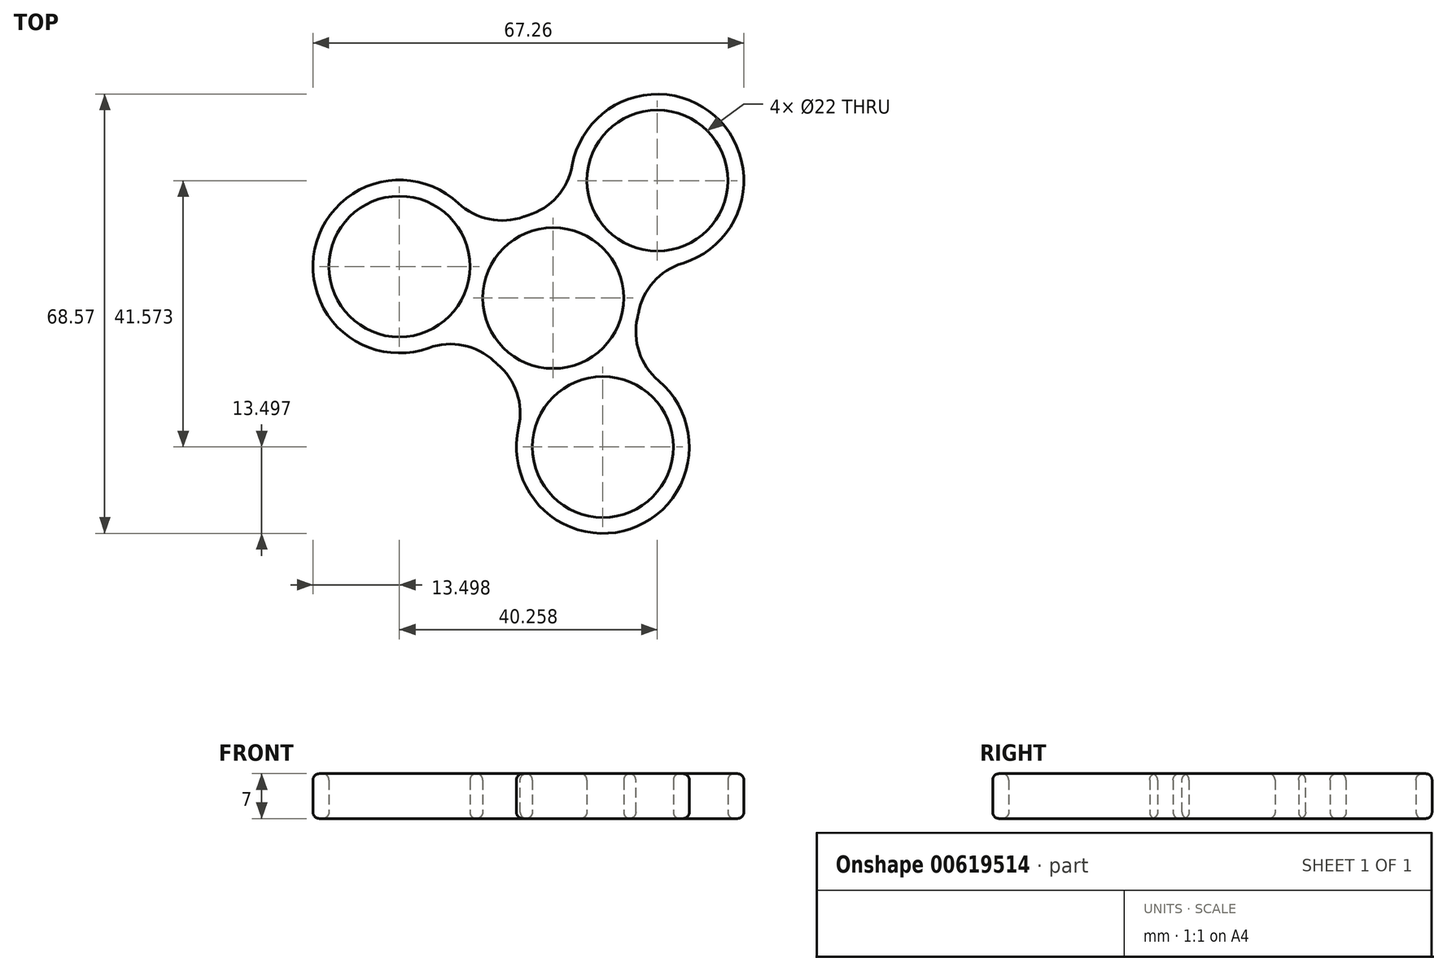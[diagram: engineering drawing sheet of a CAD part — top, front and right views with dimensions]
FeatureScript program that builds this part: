
annotation { "Feature Type Name" : "Feature", "Feature Type Description" : "" }
export const myFeature = defineFeature(function(context is Context, id is Id, definition is map)
    precondition{}
    {
        {
            var Q0;
            Q0=qCreatedBy(makeId("Top.planeOp"),FACE);
            var sketch = newSketch(context, id + "F0", { "sketchPlane" : qUnion([Q0])});
            skCircle(sketch, "E0", {"center": v(0, 0) * mm, "radius": 11 * mm});
            skCircle(sketch, "E1", {"center": v(0, 0) * mm, "radius": 13.5 * mm});
            skCircle(sketch, "E2", {"center": v(0, 0) * mm, "radius": 38 * mm});
            skCircle(sketch, "E3", {"center": v(16.26, 18.33) * mm, "radius": 13.5 * mm});
            skCircle(sketch, "E4", {"center": v(16.26, 18.33) * mm, "radius": 11 * mm});
            skCircle(sketch, "E5.1.0", {"center": v(-24, 4.91) * mm, "radius": 11 * mm});
            skCircle(sketch, "E5.1.1", {"center": v(-24, 4.91) * mm, "radius": 13.5 * mm});
            skCircle(sketch, "E5.2.0", {"center": v(7.75, -23.24) * mm, "radius": 11 * mm});
            skCircle(sketch, "E5.2.1", {"center": v(7.75, -23.24) * mm, "radius": 13.5 * mm});
            skSolve(sketch);
        }
        {
            var Q0;
            {var subQ0=sQuery(id+"F0.wireOp",EDGE,"E1");var subQ1=makeQuery(id+"F0.imprint","INTERSECT",VERTEX,{"derivedFrom":[subQ0,sQuery(id+"F0.wireOp",EDGE,"E5.1.0")]});Q0=makeQuery(id+"F0.imprint","IMPRINT",FACE,{"disambiguationData":[TD([[makeQuery(id+"F0.imprint","IMPRINT",EDGE,{"disambiguationData":[TD([[subQ1,1.0]])],"derivedFrom":subQ0}),1.0]])]});}
            var Q1;
            {var subQ0=sQuery(id+"F0.wireOp",EDGE,"E1");var subQ1=makeQuery(id+"F0.imprint","INTERSECT",VERTEX,{"derivedFrom":[subQ0,sQuery(id+"F0.wireOp",EDGE,"E4")]});Q1=makeQuery(id+"F0.imprint","IMPRINT",FACE,{"disambiguationData":[TD([[makeQuery(id+"F0.imprint","IMPRINT",EDGE,{"disambiguationData":[TD([[subQ1,1.0]])],"derivedFrom":subQ0}),1.0]])]});}
            var Q2;
            {var subQ4=sQuery(id+"F0.wireOp",EDGE,"E4");Q2=makeQuery(id+"F0.imprint","IMPRINT",FACE,{"disambiguationData":[TD([[makeQuery(id+"F0.imprint","IMPRINT",EDGE,{"derivedFrom":subQ4}),-1.0]])]});}
            var Q3;
            {var subQ0=sQuery(id+"F0.wireOp",EDGE,"E5.1.1");var subQ1=sQuery(id+"F0.wireOp",EDGE,"E0");var subQ2=makeQuery(id+"F0.imprint","INTERSECT",VERTEX,{"derivedFrom":[subQ1,subQ0]});Q3=makeQuery(id+"F0.imprint","IMPRINT",FACE,{"disambiguationData":[TD([[makeQuery(id+"F0.imprint","IMPRINT",EDGE,{"disambiguationData":[TD([[subQ2,1.0]])],"derivedFrom":subQ1}),-1.0]])]});}
            var Q4;
            {var subQ0=sQuery(id+"F0.wireOp",EDGE,"E5.1.0");Q4=makeQuery(id+"F0.imprint","IMPRINT",FACE,{"disambiguationData":[TD([[makeQuery(id+"F0.imprint","IMPRINT",EDGE,{"derivedFrom":subQ0}),-1.0]])]});}
            var Q5;
            {var subQ0=sQuery(id+"F0.wireOp",EDGE,"E1");var subQ1=makeQuery(id+"F0.imprint","INTERSECT",VERTEX,{"derivedFrom":[subQ0,sQuery(id+"F0.wireOp",EDGE,"E5.2.0")]});Q5=makeQuery(id+"F0.imprint","IMPRINT",FACE,{"disambiguationData":[TD([[makeQuery(id+"F0.imprint","IMPRINT",EDGE,{"disambiguationData":[TD([[subQ1,1.0]])],"derivedFrom":subQ0}),1.0]])]});}
            var Q6;
            {var subQ0=sQuery(id+"F0.wireOp",EDGE,"E3");var subQ1=sQuery(id+"F0.wireOp",EDGE,"E0");var subQ2=makeQuery(id+"F0.imprint","INTERSECT",VERTEX,{"derivedFrom":[subQ1,subQ0]});Q6=makeQuery(id+"F0.imprint","IMPRINT",FACE,{"disambiguationData":[TD([[makeQuery(id+"F0.imprint","IMPRINT",EDGE,{"disambiguationData":[TD([[subQ2,1.0]])],"derivedFrom":subQ1}),-1.0]])]});}
            var Q7;
            {var subQ0=sQuery(id+"F0.wireOp",EDGE,"E5.1.1");var subQ1=sQuery(id+"F0.wireOp",EDGE,"E0");var subQ2=makeQuery(id+"F0.imprint","INTERSECT",VERTEX,{"derivedFrom":[subQ1,subQ0]});Q7=makeQuery(id+"F0.imprint","IMPRINT",FACE,{"disambiguationData":[TD([[makeQuery(id+"F0.imprint","IMPRINT",EDGE,{"disambiguationData":[TD([[subQ2,-1.0]])],"derivedFrom":subQ1}),-1.0]])]});}
            var Q8;
            {var subQ4=sQuery(id+"F0.wireOp",EDGE,"E5.2.0");Q8=makeQuery(id+"F0.imprint","IMPRINT",FACE,{"disambiguationData":[TD([[makeQuery(id+"F0.imprint","IMPRINT",EDGE,{"derivedFrom":subQ4}),-1.0]])]});}
            extrude(context, id + "F1", {"entities" : qUnion([Q0, Q1, Q2, Q3, Q4, Q5, Q6, Q7, Q8]), "depth" : 7 * mm, "offsetDistance" : 25 * mm});
        }
        {
            var Q0;
            {var subQ0=sQuery(id+"F0.wireOp",EDGE,"E3");var subQ1=sQuery(id+"F0.wireOp",EDGE,"E1");Q0=makeQuery(id+"F1.opExtrude","SWEPT_EDGE",EDGE,{"disambiguationData":[OSD([subQ1,subQ0]),TDD([makeQuery(id+"F0.imprint","INTERSECT",VERTEX,{"disambiguationData":[OD(0.0)],"derivedFrom":[subQ1,subQ0]})])]});}
            var Q1;
            {var subQ0=sQuery(id+"F0.wireOp",EDGE,"E5.2.1");var subQ1=sQuery(id+"F0.wireOp",EDGE,"E1");Q1=makeQuery(id+"F1.opExtrude","SWEPT_EDGE",EDGE,{"disambiguationData":[OSD([subQ1,subQ0]),TDD([makeQuery(id+"F0.imprint","INTERSECT",VERTEX,{"disambiguationData":[OD(1.0)],"derivedFrom":[subQ1,subQ0]})])]});}
            var Q2;
            {var subQ0=sQuery(id+"F0.wireOp",EDGE,"E5.2.1");var subQ1=sQuery(id+"F0.wireOp",EDGE,"E1");Q2=makeQuery(id+"F1.opExtrude","SWEPT_EDGE",EDGE,{"disambiguationData":[OSD([subQ1,subQ0]),TDD([makeQuery(id+"F0.imprint","INTERSECT",VERTEX,{"disambiguationData":[OD(0.0)],"derivedFrom":[subQ1,subQ0]})])]});}
            var Q3;
            {var subQ0=sQuery(id+"F0.wireOp",EDGE,"E5.1.1");var subQ1=sQuery(id+"F0.wireOp",EDGE,"E1");Q3=makeQuery(id+"F1.opExtrude","SWEPT_EDGE",EDGE,{"disambiguationData":[OSD([subQ1,subQ0]),TDD([makeQuery(id+"F0.imprint","INTERSECT",VERTEX,{"disambiguationData":[OD(1.0)],"derivedFrom":[subQ1,subQ0]})])]});}
            var Q4;
            {var subQ0=sQuery(id+"F0.wireOp",EDGE,"E5.1.1");var subQ1=sQuery(id+"F0.wireOp",EDGE,"E1");Q4=makeQuery(id+"F1.opExtrude","SWEPT_EDGE",EDGE,{"disambiguationData":[OSD([subQ1,subQ0]),TDD([makeQuery(id+"F0.imprint","INTERSECT",VERTEX,{"disambiguationData":[OD(0.0)],"derivedFrom":[subQ1,subQ0]})])]});}
            var Q5;
            {var subQ0=sQuery(id+"F0.wireOp",EDGE,"E3");var subQ1=sQuery(id+"F0.wireOp",EDGE,"E1");Q5=makeQuery(id+"F1.opExtrude","SWEPT_EDGE",EDGE,{"disambiguationData":[OSD([subQ1,subQ0]),TDD([makeQuery(id+"F0.imprint","INTERSECT",VERTEX,{"disambiguationData":[OD(1.0)],"derivedFrom":[subQ1,subQ0]})])]});}
            fillet(context, id + "F2", {"entities" : qUnion([Q0, Q1, Q2, Q3, Q4, Q5]), "radius" : 10 * mm, "tangentPropagation" : true, "allowEdgeOverflow" : false});
        }
        {
            var Q0;
            Q0=makeQuery(id+"F1.opExtrude","CAP_FACE",FACE,{"disambiguationData":[OSD([sQuery(id+"F0.wireOp",EDGE,"E0"),sQuery(id+"F0.wireOp",EDGE,"E1"),sQuery(id+"F0.wireOp",EDGE,"E3"),sQuery(id+"F0.wireOp",EDGE,"E4"),sQuery(id+"F0.wireOp",EDGE,"E5.1.0"),sQuery(id+"F0.wireOp",EDGE,"E5.1.1"),sQuery(id+"F0.wireOp",EDGE,"E5.2.0"),sQuery(id+"F0.wireOp",EDGE,"E5.2.1")])],"isStart":false});
            var Q1;
            Q1=makeQuery(id+"F1.opExtrude","CAP_FACE",FACE,{"disambiguationData":[OSD([sQuery(id+"F0.wireOp",EDGE,"E0"),sQuery(id+"F0.wireOp",EDGE,"E1"),sQuery(id+"F0.wireOp",EDGE,"E3"),sQuery(id+"F0.wireOp",EDGE,"E4"),sQuery(id+"F0.wireOp",EDGE,"E5.1.0"),sQuery(id+"F0.wireOp",EDGE,"E5.1.1"),sQuery(id+"F0.wireOp",EDGE,"E5.2.0"),sQuery(id+"F0.wireOp",EDGE,"E5.2.1")])],"isStart":true});
            fillet(context, id + "F3", {"entities" : qUnion([Q0, Q1]), "radius" : 1 * mm, "tangentPropagation" : true, "allowEdgeOverflow" : false});
        }
    });
